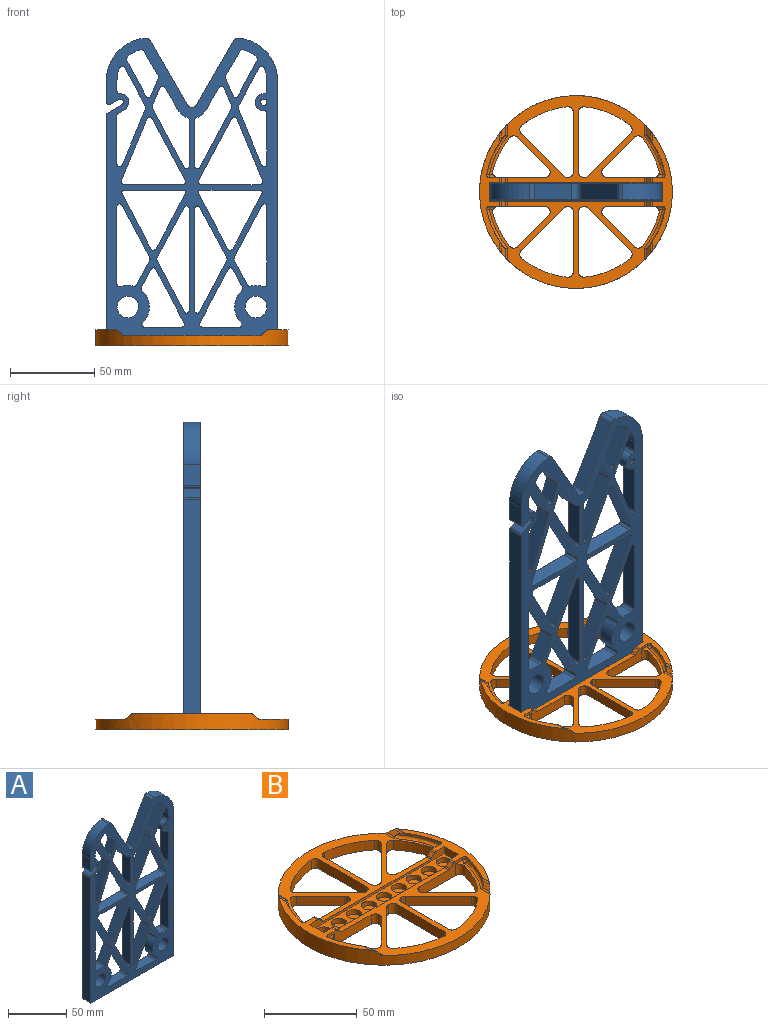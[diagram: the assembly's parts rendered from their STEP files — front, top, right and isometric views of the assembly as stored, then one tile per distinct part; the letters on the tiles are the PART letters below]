
ASSEMBLY  parts=2 mates=1
PART A: 148 faces, bbox 101.6x9.5x177.7 mm
  f0: plane 9.53x4.92mm, normal (0.5,0,-0.87), area 54.1mm2, adj f1,f5,f6,f146
  f1: cylinder r=1.91mm len=9.53mm, axis (0,-1,0), area 57mm2, adj f0,f2,f5,f6
  f2: plane 9.53x8.41mm, normal (-0.5,0,0.87), area 92.5mm2, adj f1,f5,f6,f147
  f3: plane 9.53x3.65mm, normal (0.5,0,-0.87), area 40.2mm2, adj f4,f5,f6,f144
  f4: cylinder r=5.08mm len=9.53mm, axis (0,-1,0), area 129mm2, adj f3,f5,f6,f145
  f5: plane 177.71x101.6mm, normal (0,1,0), area 6845.5mm2, adj f0,f1,f2,f3,f4,f7,f8,f9
  f6: plane 177.71x101.6mm, normal (0,-1,0), area 6845.5mm2, adj f0,f1,f2,f3,f4,f7,f8,f9
  f7: plane 28.87x9.53mm, normal (1,0,0), area 274.9mm2, adj f5,f6,f94,f144
  f8: plane 130.23x9.53mm, normal (-1,0,0), area 1240.4mm2, adj f5,f6,f142,f147
  f9: plane 9.53x6.04mm, normal (1,0,0), area 57.5mm2, adj f5,f6,f66,f145
  f10: plane 38.01x21.94mm, normal (-0.87,0,0.5), area 418mm2, adj f5,f6,f11,f82
  f11: cylinder r=3.17mm len=9.53mm, axis (0,1,0), area 63.3mm2, adj f5,f6,f10,f12
  f12: plane 38.01x21.94mm, normal (0.87,0,0.5), area 418mm2, adj f5,f6,f11,f83
  f13: plane 12.52x9.53mm, normal (-1,0,0), area 119.2mm2, adj f5,f6,f16,f146
  f14: plane 98.43x9.53mm, normal (0,0,-1), area 937.5mm2, adj f5,f6,f142,f143
  f15: plane 150.81x9.53mm, normal (1,0,0), area 1436.5mm2, adj f5,f6,f17,f143
  f16: cylinder r=25.4mm len=25.29mm, axis (0,-1,0), area 357.8mm2, adj f5,f6,f13,f83
  f17: cylinder r=25.4mm len=25.29mm, axis (0,-1,0), area 357.8mm2, adj f5,f6,f15,f82
  f18: cylinder r=6.41mm len=12.83mm, axis (0,-1,0), area 383.8mm2, adj f5,f6
  f19: cylinder r=1.91mm len=9.53mm, axis (0,-1,0), area 114mm2, adj f5,f6
  f20: plane 14.64x9.53mm, normal (0.87,0,-0.5), area 161.1mm2, adj f5,f6,f84,f87
  f21: plane 10.53x9.53mm, normal (0.92,0,0.38), area 108.6mm2, adj f5,f6,f86,f87
  f22: plane 21.2x11.37mm, normal (-0.88,0,0.47), area 229.1mm2, adj f5,f6,f85,f86
  f23: cylinder r=19.05mm len=9.53mm, axis (0,-1,0), area 87mm2, adj f5,f6,f84,f85
  f24: plane 29.96x16.07mm, normal (-0.88,0,-0.47), area 323.8mm2, adj f5,f6,f127,f129
  f25: plane 60.43x9.53mm, normal (1,0,0), area 575.6mm2, adj f5,f6,f128,f129
  f26: plane 30.47x16.07mm, normal (-0.88,0,0.47), area 328.1mm2, adj f5,f6,f127,f128
  f27: plane 60.43x9.53mm, normal (-1,0,0), area 575.6mm2, adj f5,f6,f124,f126
  f28: plane 29.96x16.07mm, normal (0.88,0,-0.47), area 323.8mm2, adj f5,f6,f125,f126
  f29: plane 30.47x16.07mm, normal (0.88,0,0.47), area 328.1mm2, adj f5,f6,f124,f125
  f30: cylinder r=12.76mm len=9.53mm, axis (0,-1,0), area 74.4mm2, adj f5,f6,f120,f123
  f31: plane 14.52x9.53mm, normal (-0.88,0,0.47), area 157mm2, adj f5,f6,f122,f123
  f32: plane 31.17x16.43mm, normal (-0.88,0,-0.47), area 335.6mm2, adj f5,f6,f121,f122
  f33: plane 46.01x9.53mm, normal (1,0,0), area 438.2mm2, adj f5,f6,f120,f121
  f34: plane 34.72x9.53mm, normal (0,0,-1), area 330.7mm2, adj f5,f6,f117,f119
  f35: plane 32.65x17.51mm, normal (0.88,0,0.47), area 352.8mm2, adj f5,f6,f118,f119
  f36: plane 32.65x17.21mm, normal (-0.88,0,0.47), area 351.5mm2, adj f5,f6,f117,f118
  f37: plane 31.95x16.85mm, normal (0.88,0,-0.47), area 344.1mm2, adj f5,f6,f138,f141
  f38: plane 22.1x9.53mm, normal (0,0,1), area 210.5mm2, adj f5,f6,f140,f141
  f39: cylinder r=12.76mm len=18.86mm, axis (0,-1,0), area 202.2mm2, adj f5,f6,f139,f140
  f40: plane 10.75x9.53mm, normal (-0.88,0,-0.47), area 116.2mm2, adj f5,f6,f138,f139
  f41: cylinder r=6.41mm len=12.83mm, axis (0,-1,0), area 383.8mm2, adj f5,f6
  f42: cylinder r=12.76mm len=18.86mm, axis (0,-1,0), area 202.2mm2, adj f5,f6,f134,f137
  f43: plane 22.1x9.53mm, normal (0,0,1), area 210.5mm2, adj f5,f6,f136,f137
  f44: plane 31.95x16.85mm, normal (-0.88,0,-0.47), area 344.1mm2, adj f5,f6,f135,f136
  f45: plane 10.75x9.53mm, normal (0.88,0,-0.47), area 116.2mm2, adj f5,f6,f134,f135
  f46: cylinder r=12.76mm len=9.53mm, axis (0,-1,0), area 74.4mm2, adj f5,f6,f130,f133
  f47: plane 46.01x9.53mm, normal (-1,0,0), area 438.2mm2, adj f5,f6,f132,f133
  f48: plane 31.17x16.43mm, normal (0.88,0,-0.47), area 335.6mm2, adj f5,f6,f131,f132
  f49: plane 14.52x9.53mm, normal (0.88,0,0.47), area 157mm2, adj f5,f6,f130,f131
  f50: plane 10.83x9.53mm, normal (-0.92,0,-0.38), area 111.7mm2, adj f5,f6,f99,f102
  f51: plane 13.55x9.53mm, normal (0.87,0,-0.5), area 149mm2, adj f5,f6,f52,f102
  f52: cylinder r=9.53mm len=9.53mm, axis (0,-1,0), area 68.7mm2, adj f5,f6,f51,f101
  f53: plane 27.17x9.53mm, normal (1,0,0), area 258.8mm2, adj f5,f6,f100,f101
  f54: plane 34.99x18.76mm, normal (-0.88,0,0.47), area 378.1mm2, adj f5,f6,f99,f100
  f55: cylinder r=9.53mm len=9.53mm, axis (0,-1,0), area 68.7mm2, adj f5,f6,f56,f95
  f56: plane 13.55x9.53mm, normal (-0.87,0,-0.5), area 149.1mm2, adj f5,f6,f55,f98
  f57: plane 10.83x9.53mm, normal (0.92,0,-0.38), area 111.7mm2, adj f5,f6,f97,f98
  f58: plane 34.99x18.76mm, normal (0.88,0,0.47), area 378.1mm2, adj f5,f6,f96,f97
  f59: plane 27.17x9.53mm, normal (-1,0,0), area 258.8mm2, adj f5,f6,f95,f96
  f60: cylinder r=19.05mm len=9.53mm, axis (0,-1,0), area 87mm2, adj f5,f6,f88,f91
  f61: plane 21.2x11.37mm, normal (0.88,0,0.47), area 229.1mm2, adj f5,f6,f90,f91
  f62: plane 10.53x9.53mm, normal (-0.92,0,0.38), area 108.6mm2, adj f5,f6,f89,f90
  f63: plane 14.64x9.53mm, normal (-0.87,0,-0.5), area 161.1mm2, adj f5,f6,f88,f89
  f64: plane 33.56x13.91mm, normal (-0.92,0,0.38), area 346.1mm2, adj f5,f6,f93,f94
  f65: plane 23.06x12.37mm, normal (-0.88,0,-0.47), area 249.2mm2, adj f5,f6,f92,f93
  f66: cylinder r=19.05mm len=9.53mm, axis (0,-1,0), area 76.8mm2, adj f5,f6,f9,f92
  f67: plane 32.65x17.51mm, normal (-0.88,0,0.47), area 352.8mm2, adj f5,f6,f114,f116
  f68: plane 34.72x9.53mm, normal (0,0,-1), area 330.7mm2, adj f5,f6,f115,f116
  f69: plane 32.65x17.21mm, normal (0.88,0,0.47), area 351.5mm2, adj f5,f6,f114,f115
  f70: plane 36.87x19.77mm, normal (0.88,0,-0.47), area 398.5mm2, adj f5,f6,f111,f113
  f71: plane 35.05x9.53mm, normal (0,0,1), area 333.9mm2, adj f5,f6,f112,f113
  f72: plane 36.87x15.28mm, normal (-0.92,0,-0.38), area 380.2mm2, adj f5,f6,f111,f112
  f73: plane 35.05x9.53mm, normal (0,0,1), area 333.9mm2, adj f5,f6,f108,f110
  f74: plane 36.87x19.77mm, normal (-0.88,0,-0.47), area 398.5mm2, adj f5,f6,f109,f110
  f75: plane 36.87x15.28mm, normal (0.92,0,-0.38), area 380.2mm2, adj f5,f6,f108,f109
  f76: cylinder r=5.08mm len=10.16mm, axis (0,-1,0), area 156.6mm2, adj f5,f6,f103,f107
  f77: plane 9.53x6.04mm, normal (-1,0,0), area 57.5mm2, adj f5,f6,f78,f107
  f78: cylinder r=19.05mm len=9.53mm, axis (0,-1,0), area 76.8mm2, adj f5,f6,f77,f106
  f79: plane 23.06x12.37mm, normal (0.88,0,-0.47), area 249.2mm2, adj f5,f6,f105,f106
  f80: plane 33.56x13.91mm, normal (0.92,0,0.38), area 346mm2, adj f5,f6,f104,f105
  f81: plane 30.09x9.53mm, normal (-1,0,0), area 286.6mm2, adj f5,f6,f103,f104
  f82: cylinder r=3.17mm len=9.53mm, axis (0,-1,0), area 34.5mm2, adj f5,f6,f10,f17
  f83: cylinder r=3.17mm len=9.53mm, axis (0,-1,0), area 34.5mm2, adj f5,f6,f12,f16
  f84: cylinder r=1.59mm len=9.53mm, axis (0,-1,0), area 19.8mm2, adj f5,f6,f20,f23
  f85: cylinder r=1.59mm len=9.53mm, axis (0,-1,0), area 20mm2, adj f5,f6,f22,f23
  f86: cylinder r=1.59mm len=9.53mm, axis (0,1,0), area 34.1mm2, adj f5,f6,f21,f22
  f87: cylinder r=1.59mm len=9.53mm, axis (0,-1,0), area 13.9mm2, adj f5,f6,f20,f21
  f88: cylinder r=1.59mm len=9.53mm, axis (0,-1,0), area 19.8mm2, adj f5,f6,f60,f63
  f89: cylinder r=1.59mm len=9.53mm, axis (0,1,0), area 13.9mm2, adj f5,f6,f62,f63
  f90: cylinder r=1.59mm len=9.53mm, axis (0,1,0), area 34.1mm2, adj f5,f6,f61,f62
  f91: cylinder r=1.59mm len=9.53mm, axis (0,-1,0), area 20mm2, adj f5,f6,f60,f61
  f92: cylinder r=1.59mm len=9.53mm, axis (0,-1,0), area 33.7mm2, adj f5,f6,f65,f66
  f93: cylinder r=1.59mm len=9.53mm, axis (0,-1,0), area 13.4mm2, adj f5,f6,f64,f65
  f94: cylinder r=1.59mm len=9.53mm, axis (0,1,0), area 41.6mm2, adj f5,f6,f7,f64
  f95: cylinder r=1.59mm len=9.53mm, axis (0,-1,0), area 19.4mm2, adj f5,f6,f55,f59
  f96: cylinder r=1.59mm len=9.53mm, axis (0,-1,0), area 40.1mm2, adj f5,f6,f58,f59
  f97: cylinder r=1.59mm len=9.53mm, axis (0,-1,0), area 13.4mm2, adj f5,f6,f57,f58
  f98: cylinder r=1.59mm len=9.53mm, axis (0,-1,0), area 33.6mm2, adj f5,f6,f56,f57
  f99: cylinder r=1.59mm len=9.53mm, axis (0,-1,0), area 13.4mm2, adj f5,f6,f50,f54
  f100: cylinder r=1.59mm len=9.53mm, axis (0,1,0), area 40.1mm2, adj f5,f6,f53,f54
  f101: cylinder r=1.59mm len=9.53mm, axis (0,-1,0), area 19.4mm2, adj f5,f6,f52,f53
  f102: cylinder r=1.59mm len=9.53mm, axis (0,1,0), area 33.6mm2, adj f5,f6,f50,f51
  f103: cylinder r=1.59mm len=9.53mm, axis (0,-1,0), area 24.5mm2, adj f5,f6,f76,f81
  f104: cylinder r=1.59mm len=9.53mm, axis (0,1,0), area 41.6mm2, adj f5,f6,f80,f81
  f105: cylinder r=1.59mm len=9.53mm, axis (0,-1,0), area 13.4mm2, adj f5,f6,f79,f80
  f106: cylinder r=1.59mm len=9.53mm, axis (0,-1,0), area 33.7mm2, adj f5,f6,f78,f79
  f107: cylinder r=1.59mm len=9.53mm, axis (0,-1,0), area 24.5mm2, adj f5,f6,f76,f77
  f108: cylinder r=1.59mm len=9.53mm, axis (0,1,0), area 29.7mm2, adj f5,f6,f73,f75
  f109: cylinder r=1.59mm len=9.53mm, axis (0,1,0), area 34.1mm2, adj f5,f6,f74,f75
  f110: cylinder r=1.59mm len=9.53mm, axis (0,1,0), area 31.2mm2, adj f5,f6,f73,f74
  f111: cylinder r=1.59mm len=9.53mm, axis (0,1,0), area 34.1mm2, adj f5,f6,f70,f72
  f112: cylinder r=1.59mm len=9.53mm, axis (0,-1,0), area 29.7mm2, adj f5,f6,f71,f72
  f113: cylinder r=1.59mm len=9.53mm, axis (0,-1,0), area 31.2mm2, adj f5,f6,f70,f71
  f114: cylinder r=1.59mm len=9.53mm, axis (0,-1,0), area 32.7mm2, adj f5,f6,f67,f69
  f115: cylinder r=1.59mm len=9.53mm, axis (0,-1,0), area 31.1mm2, adj f5,f6,f68,f69
  f116: cylinder r=1.59mm len=9.53mm, axis (0,1,0), area 31.2mm2, adj f5,f6,f67,f68
  f117: cylinder r=1.59mm len=9.53mm, axis (0,1,0), area 31.1mm2, adj f5,f6,f34,f36
  f118: cylinder r=1.59mm len=9.53mm, axis (0,-1,0), area 32.7mm2, adj f5,f6,f35,f36
  f119: cylinder r=1.59mm len=9.53mm, axis (0,-1,0), area 31.2mm2, adj f5,f6,f34,f35
  f120: cylinder r=1.59mm len=9.53mm, axis (0,-1,0), area 28.9mm2, adj f5,f6,f30,f33
  f121: cylinder r=1.59mm len=9.53mm, axis (0,1,0), area 40.2mm2, adj f5,f6,f32,f33
  f122: cylinder r=1.59mm len=9.53mm, axis (0,1,0), area 14.8mm2, adj f5,f6,f31,f32
  f123: cylinder r=1.59mm len=9.53mm, axis (0,-1,0), area 20.4mm2, adj f5,f6,f30,f31
  f124: cylinder r=1.59mm len=9.53mm, axis (0,1,0), area 40.2mm2, adj f5,f6,f27,f29
  f125: cylinder r=1.59mm len=9.53mm, axis (0,1,0), area 14.8mm2, adj f5,f6,f28,f29
  f126: cylinder r=1.59mm len=9.53mm, axis (0,1,0), area 40.1mm2, adj f5,f6,f27,f28
  f127: cylinder r=1.59mm len=9.53mm, axis (0,1,0), area 14.8mm2, adj f5,f6,f24,f26
  f128: cylinder r=1.59mm len=9.53mm, axis (0,-1,0), area 40.2mm2, adj f5,f6,f25,f26
  f129: cylinder r=1.59mm len=9.53mm, axis (0,-1,0), area 40.1mm2, adj f5,f6,f24,f25
  f130: cylinder r=1.59mm len=9.53mm, axis (0,-1,0), area 20.4mm2, adj f5,f6,f46,f49
  f131: cylinder r=1.59mm len=9.53mm, axis (0,1,0), area 14.8mm2, adj f5,f6,f48,f49
  f132: cylinder r=1.59mm len=9.53mm, axis (0,1,0), area 40.2mm2, adj f5,f6,f47,f48
  f133: cylinder r=1.59mm len=9.53mm, axis (0,-1,0), area 28.9mm2, adj f5,f6,f46,f47
  f134: cylinder r=1.59mm len=9.53mm, axis (0,-1,0), area 20.4mm2, adj f5,f6,f42,f45
  f135: cylinder r=1.59mm len=9.53mm, axis (0,-1,0), area 32.7mm2, adj f5,f6,f44,f45
  f136: cylinder r=1.59mm len=9.53mm, axis (0,1,0), area 31.1mm2, adj f5,f6,f43,f44
  f137: cylinder r=1.59mm len=9.53mm, axis (0,-1,0), area 36mm2, adj f5,f6,f42,f43
  f138: cylinder r=1.59mm len=9.53mm, axis (0,-1,0), area 32.7mm2, adj f5,f6,f37,f40
  f139: cylinder r=1.59mm len=9.53mm, axis (0,-1,0), area 20.4mm2, adj f5,f6,f39,f40
  f140: cylinder r=1.59mm len=9.53mm, axis (0,-1,0), area 36mm2, adj f5,f6,f38,f39
  f141: cylinder r=1.59mm len=9.53mm, axis (0,1,0), area 31.1mm2, adj f5,f6,f37,f38
  f142: cylinder r=1.59mm len=9.53mm, axis (0,1,0), area 23.8mm2, adj f5,f6,f8,f14
  f143: cylinder r=1.59mm len=9.53mm, axis (0,-1,0), area 23.8mm2, adj f5,f6,f14,f15
  f144: cylinder r=1.59mm len=9.53mm, axis (0,-1,0), area 15.8mm2, adj f3,f5,f6,f7
  f145: cylinder r=1.59mm len=9.53mm, axis (0,-1,0), area 24.5mm2, adj f4,f5,f6,f9
  f146: cylinder r=1.59mm len=9.53mm, axis (0,-1,0), area 31.7mm2, adj f0,f5,f6,f13
  f147: cylinder r=1.59mm len=9.53mm, axis (0,-1,0), area 15.8mm2, adj f2,f5,f6,f8
PART B: 133 faces, bbox 114.7x114.3x9.6 mm
  f0: plane 70.18x12.04mm, normal (0,0,1), area 301.4mm2, adj f1,f2,f3,f63,f65,f66,f69,f70
  f1: cylinder r=57.15mm len=114.3mm, axis (0,0,-1), area 2804.3mm2, adj f0,f12,f61,f72,f74,f76,f78,f80
  f2: plane 102.24x4.76mm, normal (0,-1,0), area 214.7mm2, adj f0,f12,f64,f67,f70,f72,f77,f81
  f3: plane 102.24x4.76mm, normal (0,1,0), area 214.7mm2, adj f0,f12,f64,f68,f69,f74,f75,f79
  f4: plane 6.35x0.25mm, normal (0,1,0), area 1.6mm2, adj f35,f36,f61,f72
  f5: plane 6.35x0.25mm, normal (0,1,0), area 1.6mm2, adj f59,f60,f61,f72
  f6: plane 32.91x9.53mm, normal (0,1,0), area 194.5mm2, adj f12,f54,f55,f61,f72,f81,f85,f93
  f7: plane 6.35x0.25mm, normal (0,-1,0), area 1.6mm2, adj f43,f46,f61,f74
  f8: plane 6.35x0.25mm, normal (0,-1,0), area 1.6mm2, adj f47,f50,f61,f74
  f9: plane 32.91x9.53mm, normal (0,-1,0), area 194.5mm2, adj f12,f51,f53,f61,f74,f79,f83,f92
  f10: cylinder r=53.98mm len=22.34mm, axis (0,0,1), area 37mm2, adj f12,f82,f86,f101,f123
  f11: cylinder r=53.98mm len=22.34mm, axis (0,0,1), area 37mm2, adj f12,f80,f84,f99,f127
  f12: plane 70.18x12.04mm, normal (0,0,1), area 301.4mm2, adj f1,f2,f3,f6,f9,f10,f11,f62
  f13: plane 25.13x25.13mm, normal (0.71,0.71,0), area 225.6mm2, adj f57,f60,f61,f72
  f14: plane 35.64x6.35mm, normal (-1,0,0), area 226.3mm2, adj f58,f59,f61,f72
  f15: cylinder r=50.8mm len=27.07mm, axis (0,0,1), area 188.7mm2, adj f57,f58,f61,f72
  f16: plane 18.39x18.39mm, normal (0.71,0.71,0), area 165.2mm2, adj f41,f42,f61,f74
  f17: cylinder r=50.8mm len=19.62mm, axis (0,0,1), area 140.6mm2, adj f40,f41,f61,f74
  f18: plane 18.39x18.39mm, normal (0.71,-0.71,0), area 165.2mm2, adj f37,f39,f61,f72
  f19: cylinder r=50.8mm len=19.62mm, axis (0,0,1), area 140.6mm2, adj f37,f38,f61,f72
  f20: plane 35.64x6.35mm, normal (1,0,0), area 226.3mm2, adj f33,f36,f61,f72
  f21: plane 25.13x25.13mm, normal (-0.71,0.71,0), area 225.6mm2, adj f34,f35,f61,f72
  f22: cylinder r=50.8mm len=27.07mm, axis (0,0,1), area 188.7mm2, adj f33,f34,f61,f72
  f23: cylinder r=50.8mm len=19.62mm, axis (0,0,1), area 140.6mm2, adj f54,f56,f61,f72
  f24: plane 18.39x18.39mm, normal (-0.71,-0.71,0), area 165.2mm2, adj f55,f56,f61,f72
  f25: cylinder r=50.8mm len=19.62mm, axis (0,0,1), area 140.6mm2, adj f52,f53,f61,f74
  f26: plane 18.39x18.39mm, normal (-0.71,0.71,0), area 165.2mm2, adj f51,f52,f61,f74
  f27: plane 25.13x25.13mm, normal (0.71,-0.71,0), area 225.6mm2, adj f49,f50,f61,f74
  f28: cylinder r=50.8mm len=27.07mm, axis (0,0,1), area 188.7mm2, adj f48,f49,f61,f74
  f29: plane 35.64x6.35mm, normal (-1,0,0), area 226.3mm2, adj f47,f48,f61,f74
  f30: plane 35.64x6.35mm, normal (1,0,0), area 226.3mm2, adj f45,f46,f61,f74
  f31: cylinder r=50.8mm len=27.07mm, axis (0,0,1), area 188.7mm2, adj f44,f45,f61,f74
  f32: plane 25.13x25.13mm, normal (-0.71,-0.71,0), area 225.6mm2, adj f43,f44,f61,f74
  f33: cylinder r=3.17mm len=6.35mm, axis (0,0,1), area 33.7mm2, adj f20,f22,f61,f72
  f34: cylinder r=3.17mm len=6.35mm, axis (0,0,1), area 33.7mm2, adj f21,f22,f61,f72
  f35: cylinder r=3.17mm len=6.35mm, axis (0,0,-1), area 15.8mm2, adj f4,f21,f61,f72
  f36: cylinder r=3.17mm len=6.35mm, axis (0,0,1), area 31.7mm2, adj f4,f20,f61,f72
  f37: cylinder r=3.17mm len=6.35mm, axis (0,0,1), area 33.7mm2, adj f18,f19,f61,f72
  f38: cylinder r=3.17mm len=7.94mm, axis (0,0,1), area 38.7mm2, adj f19,f61,f65,f72,f126
  f39: cylinder r=3.17mm len=6.35mm, axis (0,0,1), area 47.5mm2, adj f18,f61,f65,f72
  f40: cylinder r=3.17mm len=7.94mm, axis (0,0,1), area 38.7mm2, adj f17,f61,f66,f74,f130
  f41: cylinder r=3.17mm len=6.35mm, axis (0,0,1), area 33.7mm2, adj f16,f17,f61,f74
  f42: cylinder r=3.17mm len=6.35mm, axis (0,0,1), area 47.5mm2, adj f16,f61,f66,f74
  f43: cylinder r=3.17mm len=6.35mm, axis (0,0,-1), area 15.8mm2, adj f7,f32,f61,f74
  f44: cylinder r=3.17mm len=6.35mm, axis (0,0,1), area 33.7mm2, adj f31,f32,f61,f74
  f45: cylinder r=3.17mm len=6.35mm, axis (0,0,1), area 33.7mm2, adj f30,f31,f61,f74
  f46: cylinder r=3.17mm len=6.35mm, axis (0,0,1), area 31.7mm2, adj f7,f30,f61,f74
  f47: cylinder r=3.17mm len=6.35mm, axis (0,0,-1), area 31.7mm2, adj f8,f29,f61,f74
  f48: cylinder r=3.17mm len=6.35mm, axis (0,0,1), area 33.7mm2, adj f28,f29,f61,f74
  f49: cylinder r=3.17mm len=6.35mm, axis (0,0,1), area 33.7mm2, adj f27,f28,f61,f74
  f50: cylinder r=3.17mm len=6.35mm, axis (0,0,1), area 15.8mm2, adj f8,f27,f61,f74
  f51: cylinder r=3.17mm len=6.35mm, axis (0,0,-1), area 47.5mm2, adj f9,f26,f61,f74
  f52: cylinder r=3.17mm len=6.35mm, axis (0,0,1), area 33.7mm2, adj f25,f26,f61,f74
  f53: cylinder r=3.17mm len=7.94mm, axis (0,0,1), area 38.7mm2, adj f9,f25,f61,f74,f129
  f54: cylinder r=3.17mm len=7.94mm, axis (0,0,1), area 38.7mm2, adj f6,f23,f61,f72,f121
  f55: cylinder r=3.17mm len=6.35mm, axis (0,0,-1), area 47.5mm2, adj f6,f24,f61,f72
  f56: cylinder r=3.17mm len=6.35mm, axis (0,0,1), area 33.7mm2, adj f23,f24,f61,f72
  f57: cylinder r=3.17mm len=6.35mm, axis (0,0,1), area 33.7mm2, adj f13,f15,f61,f72
  f58: cylinder r=3.17mm len=6.35mm, axis (0,0,1), area 33.7mm2, adj f14,f15,f61,f72
  f59: cylinder r=3.17mm len=6.35mm, axis (0,0,-1), area 31.7mm2, adj f5,f14,f61,f72
  f60: cylinder r=3.17mm len=6.35mm, axis (0,0,1), area 15.8mm2, adj f5,f13,f61,f72
  f61: plane 114.3x114.3mm, normal (0,0,-1), area 4750.9mm2, adj f1,f4,f5,f6,f7,f8,f9,f13
  f62: plane 10.16x4.76mm, normal (1,0,0), area 48.4mm2, adj f12,f64,f67,f68
  f63: plane 10.16x4.76mm, normal (-1,0,0), area 48.4mm2, adj f0,f64,f69,f70
  f64: plane 102.87x10.8mm, normal (0,0,1), area 628.7mm2, adj f2,f3,f62,f63,f67,f68,f69,f70
  f65: plane 32.91x9.53mm, normal (0,1,0), area 194.5mm2, adj f0,f38,f39,f61,f72,f77,f89,f96
  f66: plane 32.91x9.53mm, normal (0,-1,0), area 194.5mm2, adj f0,f40,f42,f61,f74,f75,f87,f95
  f67: cylinder r=0.32mm len=4.76mm, axis (0,0,1), area 2.4mm2, adj f2,f12,f62,f64
  f68: cylinder r=0.32mm len=4.76mm, axis (0,0,-1), area 2.4mm2, adj f3,f12,f62,f64
  f69: cylinder r=0.32mm len=4.76mm, axis (0,0,1), area 2.4mm2, adj f0,f3,f63,f64
  f70: cylinder r=0.32mm len=4.76mm, axis (0,0,-1), area 2.4mm2, adj f0,f2,f63,f64
  f71: cylinder r=53.98mm len=22.34mm, axis (0,0,1), area 37mm2, adj f0,f78,f90,f102,f124
  f72: plane 102.79x51.75mm, normal (0,0,1), area 1344.9mm2, adj f1,f2,f4,f5,f6,f13,f14,f15
  f73: cylinder r=53.98mm len=22.34mm, axis (0,0,1), area 37mm2, adj f0,f76,f88,f100,f132
  f74: plane 102.79x51.75mm, normal (0,0,1), area 1344.9mm2, adj f1,f3,f7,f8,f9,f16,f17,f25
  f75: plane 3.18x2.25mm, normal (-0.71,0,0.71), area 10.1mm2, adj f3,f66,f87,f95
  f76: plane 7.79x2.28mm, normal (-0.71,0,0.71), area 16.2mm2, adj f1,f73,f88,f94,f132
  f77: plane 3.18x2.25mm, normal (-0.71,0,0.71), area 10.1mm2, adj f2,f65,f89,f96
  f78: plane 7.79x2.28mm, normal (-0.71,0,0.71), area 16.2mm2, adj f1,f71,f90,f97,f124
  f79: plane 3.18x2.25mm, normal (0.71,0,0.71), area 10.1mm2, adj f3,f9,f83,f92
  f80: plane 7.79x2.28mm, normal (0.71,0,0.71), area 16.2mm2, adj f1,f11,f84,f91,f127
  f81: plane 3.18x2.25mm, normal (0.71,0,0.71), area 10.1mm2, adj f2,f6,f85,f93
  f82: plane 7.79x2.28mm, normal (0.71,0,0.71), area 16.2mm2, adj f1,f10,f86,f98,f123
  f83: cylinder r=1.59mm len=3.18mm, axis (0,-1,0), area 4mm2, adj f3,f9,f12,f79
  f84: cylinder r=1.59mm len=6.85mm, axis (0,-1,0), area 6.6mm2, adj f1,f11,f12,f80
  f85: cylinder r=1.59mm len=3.18mm, axis (0,-1,0), area 4mm2, adj f2,f6,f12,f81
  f86: cylinder r=1.59mm len=6.85mm, axis (0,-1,0), area 6.6mm2, adj f1,f10,f12,f82
  f87: cylinder r=1.59mm len=3.18mm, axis (0,-1,0), area 4mm2, adj f0,f3,f66,f75
  f88: cylinder r=1.59mm len=6.85mm, axis (0,-1,0), area 6.6mm2, adj f0,f1,f73,f76
  f89: cylinder r=1.59mm len=3.18mm, axis (0,-1,0), area 4mm2, adj f0,f2,f65,f77
  f90: cylinder r=1.59mm len=6.85mm, axis (0,-1,0), area 6.6mm2, adj f0,f1,f71,f78
  f91: cylinder r=1.59mm len=7.12mm, axis (0,-1,0), area 7.9mm2, adj f1,f74,f80,f127
  f92: cylinder r=1.59mm len=3.18mm, axis (0,-1,0), area 4mm2, adj f3,f9,f74,f79
  f93: cylinder r=1.59mm len=3.18mm, axis (0,-1,0), area 4mm2, adj f2,f6,f72,f81
  f94: cylinder r=1.59mm len=7.12mm, axis (0,1,0), area 7.9mm2, adj f1,f74,f76,f132
  f95: cylinder r=1.59mm len=3.18mm, axis (0,1,0), area 4mm2, adj f3,f66,f74,f75
  f96: cylinder r=1.59mm len=3.18mm, axis (0,1,0), area 4mm2, adj f2,f65,f72,f77
  f97: cylinder r=1.59mm len=7.12mm, axis (0,1,0), area 7.9mm2, adj f1,f72,f78,f124
  f98: cylinder r=1.59mm len=7.12mm, axis (0,-1,0), area 7.9mm2, adj f1,f72,f82,f123
  f99: cylinder r=1.59mm len=1.9mm, axis (0,0,1), area 4.5mm2, adj f9,f11,f12,f128
  f100: cylinder r=1.59mm len=1.9mm, axis (0,0,1), area 4.5mm2, adj f0,f66,f73,f131
  f101: cylinder r=1.59mm len=1.9mm, axis (0,0,1), area 4.5mm2, adj f6,f10,f12,f122
  f102: cylinder r=1.59mm len=1.9mm, axis (0,0,1), area 4.5mm2, adj f0,f65,f71,f125
  f103: cylinder r=4.13mm len=8.26mm, axis (0,0,1), area 80.6mm2, adj f64,f104
  f104: plane 8.26x8.26mm, normal (0,0,1), area 53.5mm2, adj f103
  f105: cylinder r=4.13mm len=8.26mm, axis (0,0,1), area 80.6mm2, adj f64,f106
  f106: plane 8.26x8.26mm, normal (0,0,1), area 53.5mm2, adj f105
  f107: cylinder r=4.13mm len=8.26mm, axis (0,0,1), area 80.6mm2, adj f64,f108
  f108: plane 8.26x8.26mm, normal (0,0,1), area 53.5mm2, adj f107
  f109: cylinder r=4.13mm len=8.26mm, axis (0,0,1), area 80.6mm2, adj f64,f110
  f110: plane 8.26x8.26mm, normal (0,0,1), area 53.5mm2, adj f109
  f111: cylinder r=4.13mm len=8.26mm, axis (0,0,1), area 80.6mm2, adj f64,f112
  f112: plane 8.26x8.26mm, normal (0,0,1), area 53.5mm2, adj f111
  f113: cylinder r=4.13mm len=8.26mm, axis (0,0,1), area 80.6mm2, adj f64,f114
  f114: plane 8.26x8.26mm, normal (0,0,1), area 53.5mm2, adj f113
  f115: cylinder r=4.13mm len=8.26mm, axis (0,0,1), area 80.6mm2, adj f64,f116
  f116: plane 8.26x8.26mm, normal (0,0,1), area 53.5mm2, adj f115
  f117: cylinder r=4.13mm len=8.26mm, axis (0,0,1), area 80.6mm2, adj f64,f118
  f118: plane 8.26x8.26mm, normal (0,0,1), area 53.5mm2, adj f117
  f119: cylinder r=4.13mm len=8.26mm, axis (0,0,1), area 80.6mm2, adj f64,f120
  f120: plane 8.26x8.26mm, normal (0,0,1), area 53.5mm2, adj f119
  f121: cylinder r=1.59mm len=5.24mm, axis (1,0,0), area 9.2mm2, adj f6,f54,f72,f122
  f122: sphere r=1.59mm, area 4.5mm2, adj f101,f121,f123
  f123: torus R=52.39mm, axis (0,0,1), area 63.7mm2, adj f10,f72,f82,f98,f122
  f124: torus R=52.39mm, axis (0,0,1), area 63.7mm2, adj f71,f72,f78,f97,f125
  f125: sphere r=1.59mm, area 4.5mm2, adj f102,f124,f126
  f126: cylinder r=1.59mm len=5.24mm, axis (1,0,0), area 9.2mm2, adj f38,f65,f72,f125
  f127: torus R=52.39mm, axis (0,0,1), area 63.7mm2, adj f11,f74,f80,f91,f128
  f128: sphere r=1.59mm, area 4.5mm2, adj f99,f127,f129
  f129: cylinder r=1.59mm len=5.24mm, axis (-1,0,0), area 9.2mm2, adj f9,f53,f74,f128
  f130: cylinder r=1.59mm len=5.24mm, axis (-1,0,0), area 9.2mm2, adj f40,f66,f74,f131
  f131: sphere r=1.59mm, area 4.5mm2, adj f100,f130,f132
  f132: torus R=52.39mm, axis (0,0,1), area 63.7mm2, adj f73,f74,f76,f94,f131
PLACE A t=(0,0,93.66)mm
PLACE B at identity
MATE fastened A.f14 <-> B.f111  axis (0,0,-1) through (0,0,4.76)mm
